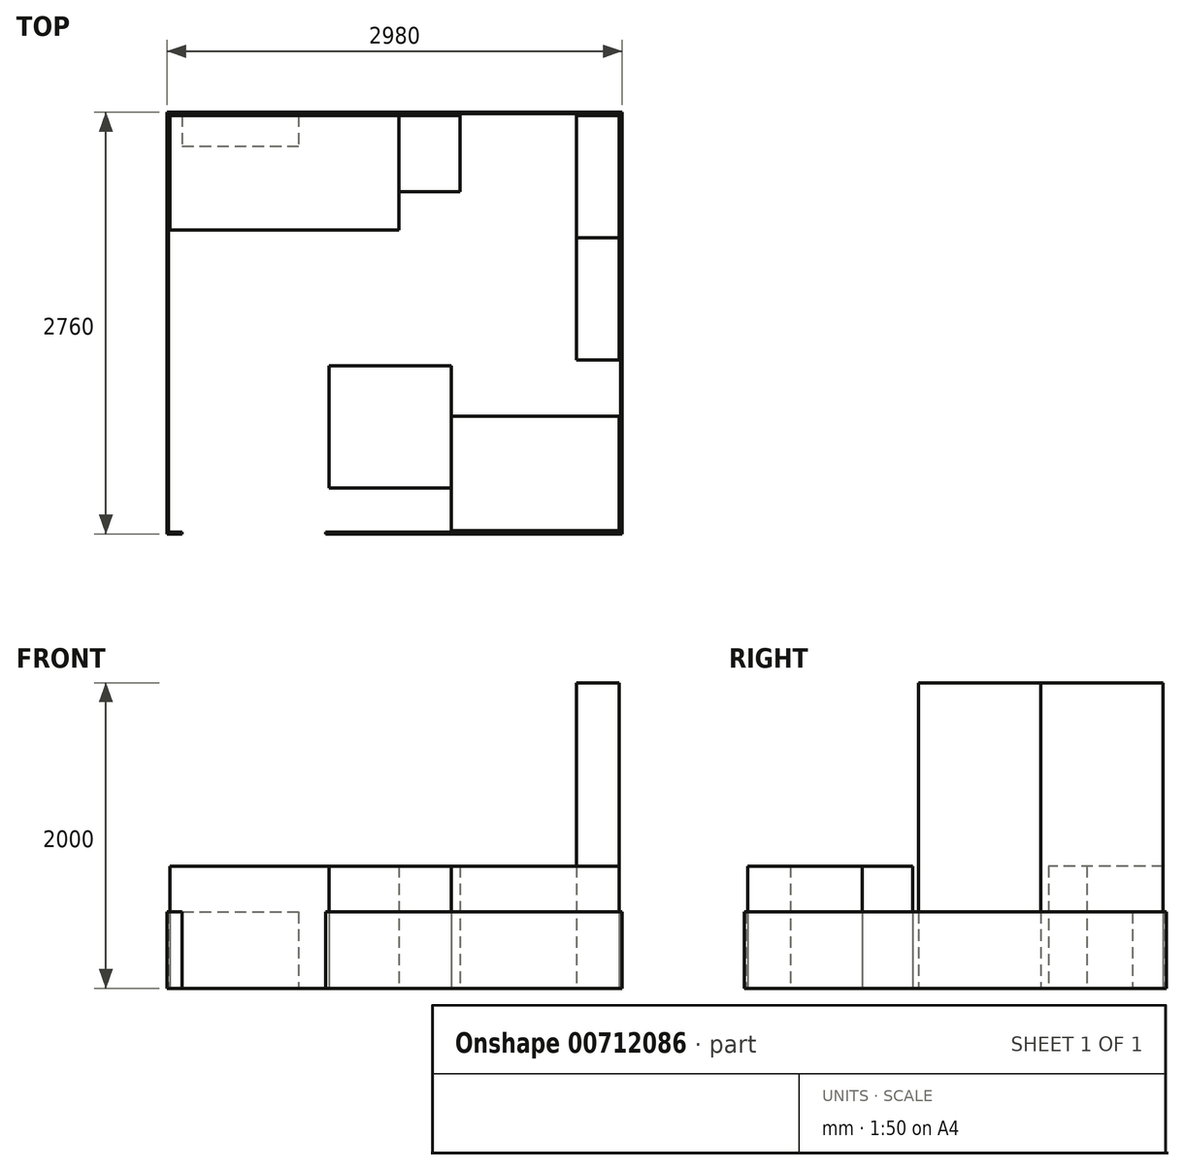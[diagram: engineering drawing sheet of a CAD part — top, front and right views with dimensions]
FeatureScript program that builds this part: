
annotation { "Feature Type Name" : "Feature", "Feature Type Description" : "" }
export const myFeature = defineFeature(function(context is Context, id is Id, definition is map)
    precondition{}
    {
        {
            var Q0;
            Q0=qCreatedBy(makeId("Top.planeOp"),FACE);
            var sketch = newSketch(context, id + "F0", { "sketchPlane" : qUnion([Q0])});
            skLineSegment(sketch, "E0.bottom", {"start": v(-1490, 1990) * mm, "end": v(1470, 1990) * mm});
            skLineSegment(sketch, "E0.top", {"start": v(-1490, -750) * mm, "end": v(-1400, -750) * mm});
            skLineSegment(sketch, "E0.left", {"start": v(-1490, 1990) * mm, "end": v(-1490, -750) * mm});
            skLineSegment(sketch, "E0.right", {"start": v(1470, 1990) * mm, "end": v(1470, -750) * mm});
            skLineSegment(sketch, "E1.0", {"start": v(-1500, 2000) * mm, "end": v(-1500, -760) * mm});
            skLineSegment(sketch, "E1.1", {"start": v(-1500, 2000) * mm, "end": v(1480, 2000) * mm});
            skLineSegment(sketch, "E1.2", {"start": v(1480, 2000) * mm, "end": v(1480, -760) * mm});
            skLineSegment(sketch, "E1.3", {"start": v(-1500, -760) * mm, "end": v(-1400, -760) * mm});
            skLineSegment(sketch, "E2", {"start": v(-1400, -750) * mm, "end": v(-1400, -760) * mm});
            skLineSegment(sketch, "E3", {"start": v(-460, -750) * mm, "end": v(-460, -760) * mm});
            skLineSegment(sketch, "E4.trimOffspring", {"start": v(-460, -750) * mm, "end": v(1470, -750) * mm});
            skLineSegment(sketch, "E5.trimOffspring", {"start": v(-460, -760) * mm, "end": v(1480, -760) * mm});
            skLineSegment(sketch, "E6.bottom", {"start": v(360, 10) * mm, "end": v(1460, 10) * mm});
            skLineSegment(sketch, "E6.top", {"start": v(360, -740) * mm, "end": v(1460, -740) * mm});
            skLineSegment(sketch, "E6.left", {"start": v(360, 10) * mm, "end": v(360, -740) * mm});
            skLineSegment(sketch, "E6.right", {"start": v(1460, 10) * mm, "end": v(1460, -740) * mm});
            skLineSegment(sketch, "E7.bottom", {"start": v(1180, 380) * mm, "end": v(1460, 380) * mm});
            skLineSegment(sketch, "E7.top", {"start": v(1180, 1180) * mm, "end": v(1460, 1180) * mm});
            skLineSegment(sketch, "E7.left", {"start": v(1180, 380) * mm, "end": v(1180, 1180) * mm});
            skLineSegment(sketch, "E7.right", {"start": v(1460, 380) * mm, "end": v(1460, 1180) * mm});
            skLineSegment(sketch, "E8.bottom", {"start": v(1180, 1980) * mm, "end": v(1460, 1980) * mm});
            skLineSegment(sketch, "E8.left", {"start": v(1180, 1980) * mm, "end": v(1180, 1180) * mm});
            skLineSegment(sketch, "E8.right", {"start": v(1460, 1980) * mm, "end": v(1460, 1180) * mm});
            skLineSegment(sketch, "E9.bottom", {"start": v(-440, -460) * mm, "end": v(360, -460) * mm});
            skLineSegment(sketch, "E9.top", {"start": v(-440, 340) * mm, "end": v(360, 340) * mm});
            skLineSegment(sketch, "E9.left", {"start": v(-440, -460) * mm, "end": v(-440, 340) * mm});
            skLineSegment(sketch, "E9.right", {"start": v(360, -460) * mm, "end": v(360, 340) * mm});
            skLineSegment(sketch, "E10.bottom", {"start": v(-1400, 1980) * mm, "end": v(-640, 1980) * mm});
            skLineSegment(sketch, "E10.top", {"start": v(-1400, 1780) * mm, "end": v(-640, 1780) * mm});
            skLineSegment(sketch, "E10.left", {"start": v(-1400, 1980) * mm, "end": v(-1400, 1780) * mm});
            skLineSegment(sketch, "E10.right", {"start": v(-640, 1980) * mm, "end": v(-640, 1780) * mm});
            skLineSegment(sketch, "E11.bottom", {"start": v(-1480, 1980) * mm, "end": v(20, 1980) * mm});
            skLineSegment(sketch, "E11.top", {"start": v(-1480, 1230) * mm, "end": v(20, 1230) * mm});
            skLineSegment(sketch, "E11.left", {"start": v(-1480, 1980) * mm, "end": v(-1480, 1230) * mm});
            skLineSegment(sketch, "E11.right", {"start": v(20, 1980) * mm, "end": v(20, 1230) * mm});
            skLineSegment(sketch, "E12.bottom", {"start": v(20, 1480) * mm, "end": v(420, 1480) * mm});
            skLineSegment(sketch, "E12.top", {"start": v(20, 1980) * mm, "end": v(420, 1980) * mm});
            skLineSegment(sketch, "E12.left", {"start": v(20, 1480) * mm, "end": v(20, 1980) * mm});
            skLineSegment(sketch, "E12.right", {"start": v(420, 1480) * mm, "end": v(420, 1980) * mm});
            skSolve(sketch);
        }
        {
            var Q0;
            Q0=makeQuery(id+"F0.imprint","IMPRINT",FACE,{"disambiguationData":[TD([[makeQuery(id+"F0.imprint","IMPRINT",EDGE,{"derivedFrom":sQuery(id+"F0.wireOp",EDGE,"E0.bottom")}),1.0]])]});
            extrude(context, id + "F1", {"entities" : qUnion([Q0]), "depth" : 500 * mm, "offsetDistance" : 25 * mm});
        }
        {
            var Q0;
            Q0=makeQuery(id+"F0.imprint","IMPRINT",FACE,{"disambiguationData":[TD([[makeQuery(id+"F0.imprint","IMPRINT",EDGE,{"derivedFrom":sQuery(id+"F0.wireOp",EDGE,"E7.bottom")}),1.0]])]});
            extrude(context, id + "F2", {"entities" : qUnion([Q0]), "depth" : 2000 * mm, "offsetDistance" : 25 * mm});
        }
        {
            var Q0;
            Q0=makeQuery(id+"F0.imprint","IMPRINT",FACE,{"disambiguationData":[TD([[makeQuery(id+"F0.imprint","IMPRINT",EDGE,{"derivedFrom":sQuery(id+"F0.wireOp",EDGE,"E10.top")}),1.0]])]});
            extrude(context, id + "F3", {"entities" : qUnion([Q0]), "depth" : 500 * mm, "offsetDistance" : 25 * mm});
        }
        {
            var Q0;
            Q0=makeQuery(id+"F0.imprint","IMPRINT",FACE,{"disambiguationData":[TD([[makeQuery(id+"F0.imprint","IMPRINT",EDGE,{"derivedFrom":sQuery(id+"F0.wireOp",EDGE,"E11.bottom")}),-1.0]])]});
            var Q1;
            {var subQ2=sQuery(id+"F0.wireOp",EDGE,"E10.left");Q1=makeQuery(id+"F0.imprint","IMPRINT",FACE,{"disambiguationData":[TD([[makeQuery(id+"F0.imprint","IMPRINT",EDGE,{"derivedFrom":subQ2}),-1.0]])]});}
            var Q2;
            Q2=makeQuery(id+"F0.imprint","IMPRINT",FACE,{"disambiguationData":[TD([[makeQuery(id+"F0.imprint","IMPRINT",EDGE,{"derivedFrom":sQuery(id+"F0.wireOp",EDGE,"E10.top")}),1.0]])]});
            extrude(context, id + "F4", {"entities" : qUnion([Q0, Q1, Q2]), "depth" : 800 * mm, "offsetDistance" : 25 * mm});
        }
        {
            var Q0;
            Q0=makeQuery(id+"F0.imprint","IMPRINT",FACE,{"disambiguationData":[TD([[makeQuery(id+"F0.imprint","IMPRINT",EDGE,{"derivedFrom":sQuery(id+"F0.wireOp",EDGE,"E9.bottom")}),1.0]])]});
            extrude(context, id + "F5", {"entities" : qUnion([Q0]), "depth" : 800 * mm, "offsetDistance" : 25 * mm});
        }
        {
            var Q0;
            Q0=makeQuery(id+"F0.imprint","IMPRINT",FACE,{"disambiguationData":[TD([[makeQuery(id+"F0.imprint","IMPRINT",EDGE,{"derivedFrom":sQuery(id+"F0.wireOp",EDGE,"E6.bottom")}),-1.0]])]});
            extrude(context, id + "F6", {"entities" : qUnion([Q0]), "depth" : 800 * mm, "offsetDistance" : 25 * mm});
        }
        {
            var Q0;
            Q0=makeQuery(id+"F0.imprint","IMPRINT",FACE,{"disambiguationData":[TD([[makeQuery(id+"F0.imprint","IMPRINT",EDGE,{"derivedFrom":sQuery(id+"F0.wireOp",EDGE,"E8.bottom")}),-1.0]])]});
            extrude(context, id + "F7", {"entities" : qUnion([Q0]), "depth" : 2000 * mm, "offsetDistance" : 25 * mm});
        }
        {
            var Q0;
            Q0=makeQuery(id+"F0.imprint","IMPRINT",FACE,{"disambiguationData":[TD([[makeQuery(id+"F0.imprint","IMPRINT",EDGE,{"derivedFrom":sQuery(id+"F0.wireOp",EDGE,"E12.bottom")}),1.0]])]});
            extrude(context, id + "F8", {"entities" : qUnion([Q0]), "depth" : 800 * mm, "offsetDistance" : 25 * mm});
        }
    });
